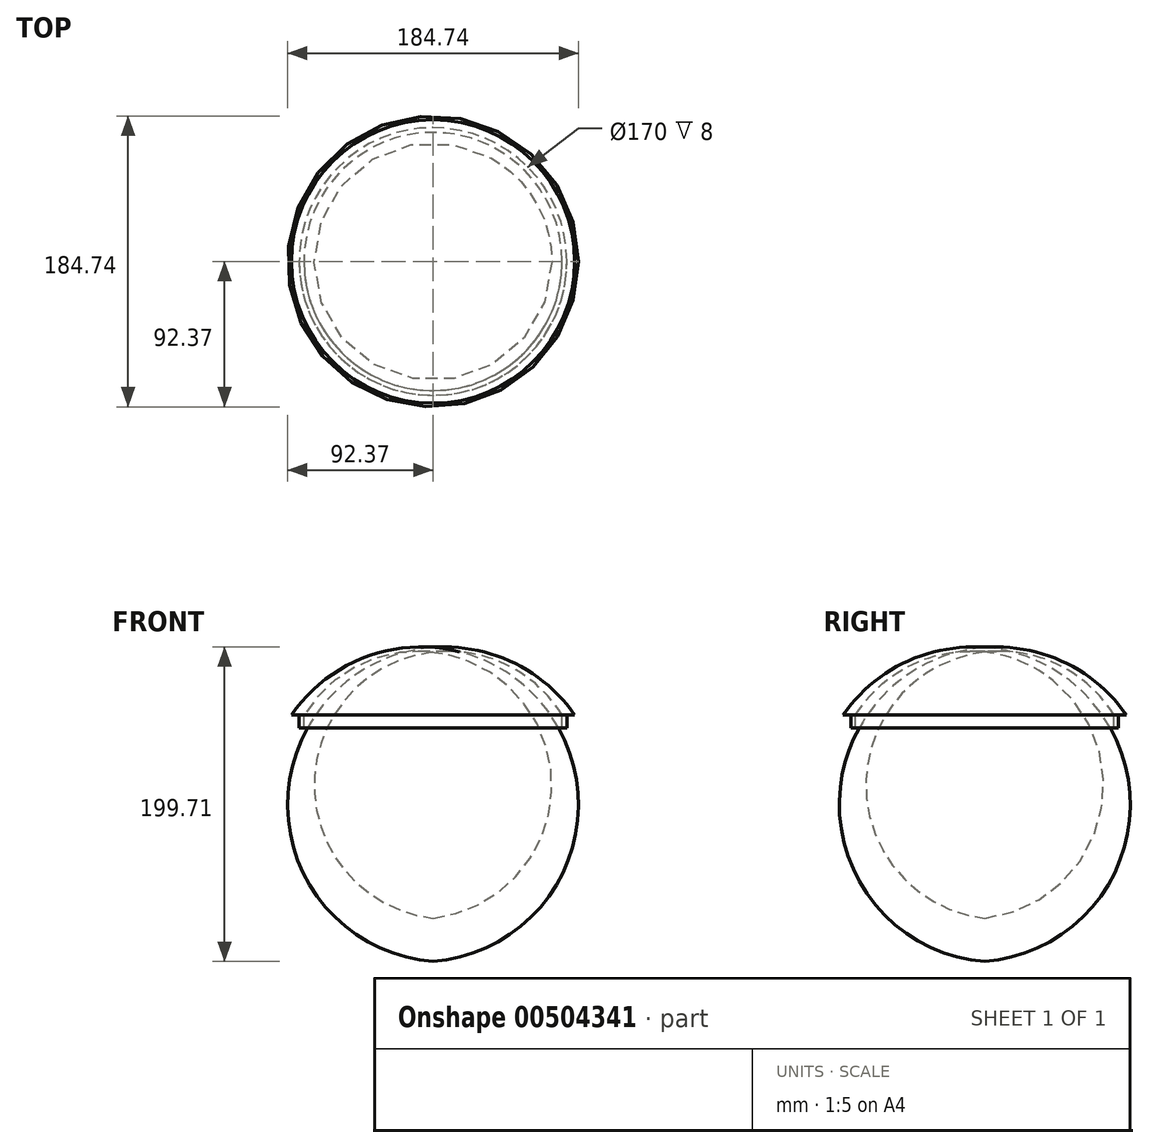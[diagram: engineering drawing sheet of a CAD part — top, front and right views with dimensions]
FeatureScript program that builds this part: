
annotation { "Feature Type Name" : "Feature", "Feature Type Description" : "" }
export const myFeature = defineFeature(function(context is Context, id is Id, definition is map)
    precondition{}
    {
        {
            var Q0;
            Q0=qCreatedBy(makeId("Top.planeOp"),FACE);
            var sketch = newSketch(context, id + "F0", { "sketchPlane" : qUnion([Q0])});
            skLineSegment(sketch, "E0", {"start": v(0, 0) * mm, "end": v(-85, 0) * mm});
            skLineSegment(sketch, "E1", {"start": v(-85, 0) * mm, "end": v(-88, 0) * mm});
            skCircle(sketch, "E2", {"center": v(0, 0) * mm, "radius": 88 * mm});
            skLineSegment(sketch, "E3", {"start": v(-88, 0) * mm, "end": v(-82, 0) * mm});
            skCircle(sketch, "E4", {"center": v(0, 0) * mm, "radius": 82 * mm});
            skCircle(sketch, "E5", {"center": v(0, 0) * mm, "radius": 85 * mm});
            skSolve(sketch);
        }
        {
            var Q0;
            Q0=qCreatedBy(makeId("Front.planeOp"),FACE);
            var sketch = newSketch(context, id + "F1", { "sketchPlane" : qUnion([Q0])});
            skLineSegment(sketch, "E6", {"start": v(0, 0) * mm, "end": v(0, 40) * mm});
            skLineSegment(sketch, "E7", {"start": v(0, 40) * mm, "end": v(0, 43) * mm});
            skLineSegment(sketch, "E8", {"start": v(0, 0) * mm, "end": v(-85, 0) * mm});
            skLineSegment(sketch, "E9", {"start": v(-85, 0) * mm, "end": v(-90, 0) * mm});
            skArc(sketch, "E10", {"start": v(0, 43) * mm, "mid": v(-50.74, 33.52) * mm, "end": v(-90, 0) * mm});
            skLineSegment(sketch, "E11", {"start": v(0, 43) * mm, "end": v(0, 35) * mm});
            skLineSegment(sketch, "E12", {"start": v(-90, 0) * mm, "end": v(-82, 0) * mm});
            skArc(sketch, "E13", {"start": v(0, 40) * mm, "mid": v(-46.82, 31.93) * mm, "end": v(-82, 0) * mm});
            skSolve(sketch);
        }
        {
            var Q0;
            {var subQ0=sQuery(id+"F1.wireOp",EDGE,"E10");Q0=makeQuery(id+"F1.imprint","IMPRINT",FACE,{"disambiguationData":[TD([[makeQuery(id+"F1.imprint","IMPRINT",EDGE,{"derivedFrom":subQ0}),1.0]])]});}
            var Q1;
            Q1=sQuery(id+"F0.wireOp",EDGE,"E4");
            revolve(context, id + "F2", {"entities" : qUnion([Q0]), "axis" : qUnion([Q1]), "revolveType" : RevolveType.FULL});
        }
        {
            var Q0;
            Q0=makeQuery(id+"F0.imprint","IMPRINT",FACE,{"disambiguationData":[TD([[makeQuery(id+"F0.imprint","IMPRINT",EDGE,{"derivedFrom":sQuery(id+"F0.wireOp",EDGE,"E4")}),-1.0]])]});
            extrude(context, id + "F3", {"entities" : qUnion([Q0]), "operationType" : NewBodyOperationType.ADD, "oppositeDirection" : true, "depth" : 8 * mm});
        }
    });
